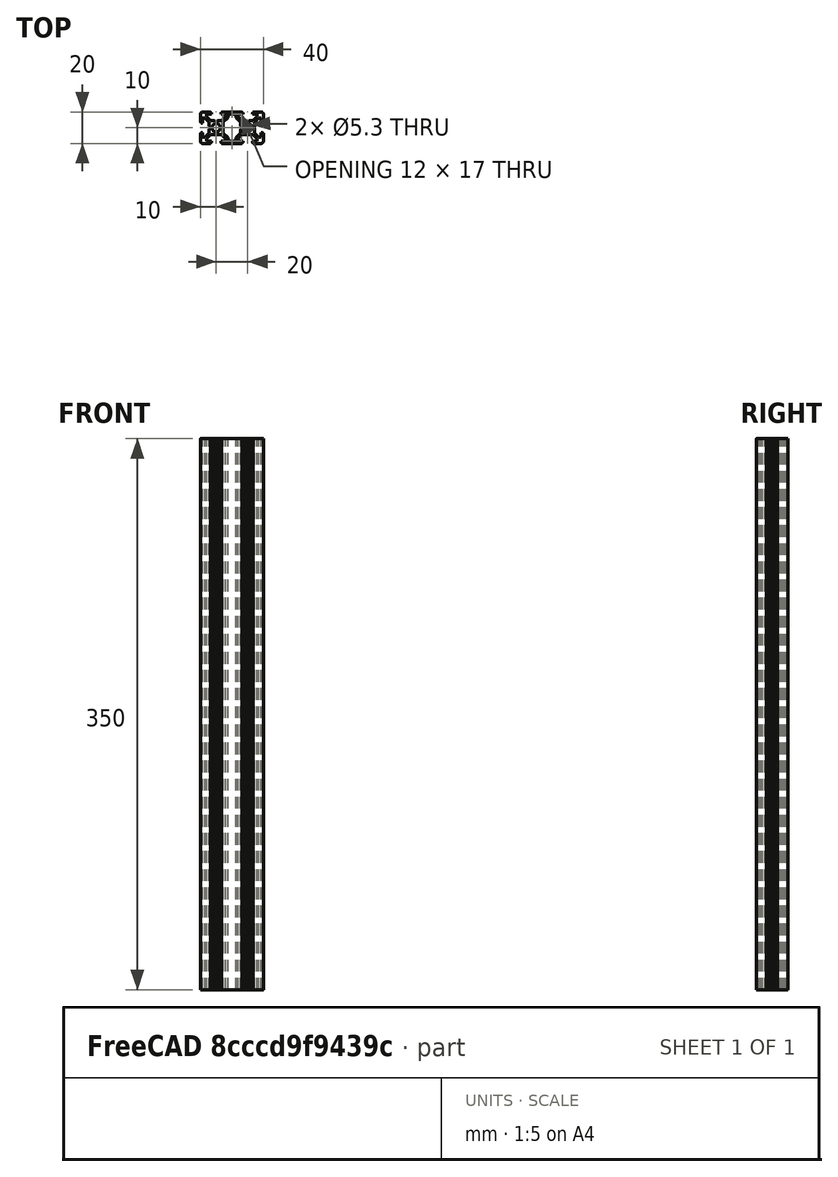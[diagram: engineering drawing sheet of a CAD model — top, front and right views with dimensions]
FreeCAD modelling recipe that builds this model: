
FCSTD DOCUMENT  (FreeCAD 0.17R13541 (Git))
Label: xx_458_aluminimum-extrusion
License: All rights reserved
LicenseURL: http://en.wikipedia.org/wiki/All_rights_reserved
objects: Sketcher::SketchObject×1, PartDesign::Pad×1, PartDesign::Body×1, Part::Feature×1
note: 5 computed .brp shape members not serialized (recipe doc carries the construction recipe); baked Part::Feature solids carry a one-line shape summary decoded from their .brp

FEATURE [Sketcher::SketchObject] Sketch516
  sketch-geometry (130):
    g0: LineSegment StartX=17.0607 StartY=-6 StartZ=0 EndX=14.5 EndY=-3.43934 EndZ=0
    g1: LineSegment StartX=16 StartY=-7.06066 StartZ=0 EndX=13.4393 EndY=-4.5 EndZ=0
    g2: LineSegment StartX=-4 StartY=-7.06066 StartZ=0 EndX=-6.56066 EndY=-4.5 EndZ=0
    g3: LineSegment StartX=6.56066 StartY=4.5 StartZ=0 EndX=4 EndY=7.06066 EndZ=0
    g4: LineSegment StartX=14.5 StartY=-0.866025 StartZ=0 EndX=14 EndY=0 EndZ=0
    g5: LineSegment StartX=-13.4393 StartY=4.5 StartZ=0 EndX=-16 EndY=7.06066 EndZ=0
    g6: LineSegment StartX=-18.5 StartY=-10 StartZ=0 EndX=-13.5 EndY=-10 EndZ=0
    g7: LineSegment StartX=13.5 StartY=-10 StartZ=0 EndX=18.5 EndY=-10 EndZ=0
    g8: LineSegment StartX=-6.5 StartY=-10 StartZ=0 EndX=6.5 EndY=-10 EndZ=0
    g9: LineSegment StartX=6 StartY=0 StartZ=0 EndX=5.5 EndY=0.866025 EndZ=0
    g10: LineSegment StartX=5.5 StartY=3.43934 StartZ=0 EndX=2.5 EndY=6.43934 EndZ=0
    g11: LineSegment StartX=-14 StartY=0 StartZ=0 EndX=-14.5 EndY=0.866025 EndZ=0
    g12: LineSegment StartX=10.866 StartY=-4.5 StartZ=0 EndX=10 EndY=-4 EndZ=0
    g13: LineSegment StartX=-9.13397 StartY=-4.5 StartZ=0 EndX=-10 EndY=-4 EndZ=0
    g14: LineSegment StartX=10 StartY=4 StartZ=0 EndX=9.13397 EndY=4.5 EndZ=0
    g15: LineSegment StartX=-10 StartY=4 StartZ=0 EndX=-10.866 EndY=4.5 EndZ=0
    g16: LineSegment StartX=-2.5 StartY=-6.43934 StartZ=0 EndX=-5.5 EndY=-3.43934 EndZ=0
    g17: LineSegment StartX=-14.5 StartY=3.43934 StartZ=0 EndX=-17.0607 EndY=6 EndZ=0
    g18: LineSegment StartX=-6.5 StartY=10 StartZ=0 EndX=6.5 EndY=10 EndZ=0
    g19: LineSegment StartX=-5.5 StartY=-0.866025 StartZ=0 EndX=-6 EndY=0 EndZ=0
    g20: LineSegment StartX=-7 StartY=-9.5 StartZ=0 EndX=-6.5 EndY=-9.5 EndZ=0
    g21: LineSegment StartX=-13.5 StartY=-9.5 StartZ=0 EndX=-13 EndY=-9.5 EndZ=0
    g22: LineSegment StartX=-16 StartY=-8.5 StartZ=0 EndX=-13 EndY=-8.5 EndZ=0
    g23: LineSegment StartX=-2.5 StartY=-8.5 StartZ=0 EndX=2.5 EndY=-8.5 EndZ=0
    g24: LineSegment StartX=13 StartY=-9.5 StartZ=0 EndX=13.5 EndY=-9.5 EndZ=0
    g25: LineSegment StartX=-18.5 StartY=-6 StartZ=0 EndX=-17.0607 EndY=-6 EndZ=0
    g26: LineSegment StartX=6.5 StartY=-9.5 StartZ=0 EndX=7 EndY=-9.5 EndZ=0
    g27: LineSegment StartX=-7 StartY=-8.5 StartZ=0 EndX=-4 EndY=-8.5 EndZ=0
    g28: LineSegment StartX=13 StartY=-8.5 StartZ=0 EndX=16 EndY=-8.5 EndZ=0
    g29: LineSegment StartX=4 StartY=-8.5 StartZ=0 EndX=7 EndY=-8.5 EndZ=0
    g30: LineSegment StartX=17.0607 StartY=-6 StartZ=0 EndX=18.5 EndY=-6 EndZ=0
    g31: LineSegment StartX=-13.4393 StartY=-4.5 StartZ=0 EndX=-10.866 EndY=-4.5 EndZ=0
    g32: LineSegment StartX=-9.13397 StartY=-4.5 StartZ=0 EndX=-6.56066 EndY=-4.5 EndZ=0
    g33: LineSegment StartX=6.56066 StartY=-4.5 StartZ=0 EndX=9.13397 EndY=-4.5 EndZ=0
    g34: LineSegment StartX=-20 StartY=-3.5 StartZ=0 EndX=-19.5 EndY=-3.5 EndZ=0
    g35: LineSegment StartX=10.866 StartY=-4.5 StartZ=0 EndX=13.4393 EndY=-4.5 EndZ=0
    g36: LineSegment StartX=19.5 StartY=-3.5 StartZ=0 EndX=20 EndY=-3.5 EndZ=0
    g37: LineSegment StartX=-19.5 StartY=-3 StartZ=0 EndX=-18.5 EndY=-3 EndZ=0
    g38: LineSegment StartX=18.5 StartY=-3 StartZ=0 EndX=19.5 EndY=-3 EndZ=0
    g39: LineSegment StartX=-19.5 StartY=3 StartZ=0 EndX=-18.5 EndY=3 EndZ=0
    g40: LineSegment StartX=18.5 StartY=3 StartZ=0 EndX=19.5 EndY=3 EndZ=0
    g41: LineSegment StartX=-20 StartY=3.5 StartZ=0 EndX=-19.5 EndY=3.5 EndZ=0
    g42: LineSegment StartX=19.5 StartY=3.5 StartZ=0 EndX=20 EndY=3.5 EndZ=0
    g43: LineSegment StartX=6.56066 StartY=4.5 StartZ=0 EndX=9.13397 EndY=4.5 EndZ=0
    g44: LineSegment StartX=-9.13397 StartY=4.5 StartZ=0 EndX=-6.56066 EndY=4.5 EndZ=0
    g45: LineSegment StartX=-13.4393 StartY=4.5 StartZ=0 EndX=-10.866 EndY=4.5 EndZ=0
    g46: LineSegment StartX=-18.5 StartY=6 StartZ=0 EndX=-17.0607 EndY=6 EndZ=0
    g47: LineSegment StartX=10.866 StartY=4.5 StartZ=0 EndX=13.4393 EndY=4.5 EndZ=0
    g48: LineSegment StartX=-16 StartY=8.5 StartZ=0 EndX=-13 EndY=8.5 EndZ=0
    g49: LineSegment StartX=17.0607 StartY=6 StartZ=0 EndX=18.5 EndY=6 EndZ=0
    g50: LineSegment StartX=4 StartY=8.5 StartZ=0 EndX=7 EndY=8.5 EndZ=0
    g51: LineSegment StartX=-7 StartY=8.5 StartZ=0 EndX=-4 EndY=8.5 EndZ=0
    g52: LineSegment StartX=-7 StartY=9.5 StartZ=0 EndX=-6.5 EndY=9.5 EndZ=0
    g53: LineSegment StartX=13 StartY=8.5 StartZ=0 EndX=16 EndY=8.5 EndZ=0
    g54: LineSegment StartX=-2.5 StartY=8.5 StartZ=0 EndX=2.5 EndY=8.5 EndZ=0
    g55: LineSegment StartX=6.5 StartY=9.5 StartZ=0 EndX=7 EndY=9.5 EndZ=0
    g56: LineSegment StartX=-13.5 StartY=9.5 StartZ=0 EndX=-13 EndY=9.5 EndZ=0
    g57: LineSegment StartX=13 StartY=9.5 StartZ=0 EndX=13.5 EndY=9.5 EndZ=0
    g58: LineSegment StartX=-18.5 StartY=10 StartZ=0 EndX=-13.5 EndY=10 EndZ=0
    g59: LineSegment StartX=13.5 StartY=10 StartZ=0 EndX=18.5 EndY=10 EndZ=0
    g60: LineSegment StartX=-10.866 StartY=-4.5 StartZ=0 EndX=-10 EndY=-4 EndZ=0
    g61: LineSegment StartX=9.13397 StartY=-4.5 StartZ=0 EndX=10 EndY=-4 EndZ=0
    g62: LineSegment StartX=10 StartY=4 StartZ=0 EndX=10.866 EndY=4.5 EndZ=0
    g63: LineSegment StartX=-10 StartY=4 StartZ=0 EndX=-9.13397 EndY=4.5 EndZ=0
    g64: LineSegment StartX=-16 StartY=-7.06066 StartZ=0 EndX=-13.4393 EndY=-4.5 EndZ=0
    g65: LineSegment StartX=-6.56066 StartY=4.5 StartZ=0 EndX=-4 EndY=7.06066 EndZ=0
    g66: LineSegment StartX=4 StartY=-7.06066 StartZ=0 EndX=6.56066 EndY=-4.5 EndZ=0
    g67: LineSegment StartX=2.5 StartY=-6.43934 StartZ=0 EndX=5.5 EndY=-3.43934 EndZ=0
    g68: LineSegment StartX=-5.5 StartY=3.43934 StartZ=0 EndX=-2.5 EndY=6.43934 EndZ=0
    g69: LineSegment StartX=14.5 StartY=3.43934 StartZ=0 EndX=17.0607 EndY=6 EndZ=0
    g70: LineSegment StartX=-17.0607 StartY=-6 StartZ=0 EndX=-14.5 EndY=-3.43934 EndZ=0
    g71: LineSegment StartX=13.4393 StartY=4.5 StartZ=0 EndX=16 EndY=7.06066 EndZ=0
    g72: LineSegment StartX=5.5 StartY=-0.866025 StartZ=0 EndX=6 EndY=0 EndZ=0
    g73: LineSegment StartX=-14.5 StartY=-0.866025 StartZ=0 EndX=-14 EndY=0 EndZ=0
    g74: LineSegment StartX=14 StartY=0 StartZ=0 EndX=14.5 EndY=0.866025 EndZ=0
    g75: LineSegment StartX=-6 StartY=0 StartZ=0 EndX=-5.5 EndY=0.866025 EndZ=0
    g76: LineSegment StartX=-20 StartY=3.5 StartZ=0 EndX=-20 EndY=8.5 EndZ=0
    g77: LineSegment StartX=-20 StartY=-8.5 StartZ=0 EndX=-20 EndY=-3.5 EndZ=0
    g78: LineSegment StartX=-19.5 StartY=-3.5 StartZ=0 EndX=-19.5 EndY=-3 EndZ=0
    g79: LineSegment StartX=-19.5 StartY=3 StartZ=0 EndX=-19.5 EndY=3.5 EndZ=0
    g80: LineSegment StartX=-16 StartY=7.06066 StartZ=0 EndX=-16 EndY=8.5 EndZ=0
    g81: LineSegment StartX=-18.5 StartY=3 StartZ=0 EndX=-18.5 EndY=6 EndZ=0
    g82: LineSegment StartX=-18.5 StartY=-6 StartZ=0 EndX=-18.5 EndY=-3 EndZ=0
    g83: LineSegment StartX=-13.5 StartY=-10 StartZ=0 EndX=-13.5 EndY=-9.5 EndZ=0
    g84: LineSegment StartX=-16 StartY=-8.5 StartZ=0 EndX=-16 EndY=-7.06066 EndZ=0
    g85: LineSegment StartX=-14.5 StartY=0.866025 StartZ=0 EndX=-14.5 EndY=3.43934 EndZ=0
    g86: LineSegment StartX=-13 StartY=8.5 StartZ=0 EndX=-13 EndY=9.5 EndZ=0
    g87: LineSegment StartX=-14.5 StartY=-3.43934 StartZ=0 EndX=-14.5 EndY=-0.866025 EndZ=0
    g88: LineSegment StartX=-13.5 StartY=9.5 StartZ=0 EndX=-13.5 EndY=10 EndZ=0
    g89: LineSegment StartX=-13 StartY=-9.5 StartZ=0 EndX=-13 EndY=-8.5 EndZ=0
    g90: LineSegment StartX=-7 StartY=8.5 StartZ=0 EndX=-7 EndY=9.5 EndZ=0
    g91: LineSegment StartX=-7 StartY=-9.5 StartZ=0 EndX=-7 EndY=-8.5 EndZ=0
    g92: LineSegment StartX=-6.5 StartY=-10 StartZ=0 EndX=-6.5 EndY=-9.5 EndZ=0
    g93: LineSegment StartX=-6.5 StartY=9.5 StartZ=0 EndX=-6.5 EndY=10 EndZ=0
    g94: LineSegment StartX=-2.5 StartY=6.43934 StartZ=0 EndX=-2.5 EndY=8.5 EndZ=0
    g95: LineSegment StartX=-5.5 StartY=-3.43934 StartZ=0 EndX=-5.5 EndY=-0.866025 EndZ=0
    g96: LineSegment StartX=-5.5 StartY=0.866025 StartZ=0 EndX=-5.5 EndY=3.43934 EndZ=0
    g97: LineSegment StartX=-4 StartY=-8.5 StartZ=0 EndX=-4 EndY=-7.06066 EndZ=0
    g98: LineSegment StartX=-4 StartY=7.06066 StartZ=0 EndX=-4 EndY=8.5 EndZ=0
    g99: LineSegment StartX=-2.5 StartY=-8.5 StartZ=0 EndX=-2.5 EndY=-6.43934 EndZ=0
    g100: LineSegment StartX=2.5 StartY=-8.5 StartZ=0 EndX=2.5 EndY=-6.43934 EndZ=0
    g101: LineSegment StartX=2.5 StartY=6.43934 StartZ=0 EndX=2.5 EndY=8.5 EndZ=0
    g102: LineSegment StartX=4 StartY=7.06066 StartZ=0 EndX=4 EndY=8.5 EndZ=0
    g103: LineSegment StartX=5.5 StartY=-3.43934 StartZ=0 EndX=5.5 EndY=-0.866025 EndZ=0
    g104: LineSegment StartX=5.5 StartY=0.866025 StartZ=0 EndX=5.5 EndY=3.43934 EndZ=0
    g105: LineSegment StartX=4 StartY=-8.5 StartZ=0 EndX=4 EndY=-7.06066 EndZ=0
    g106: LineSegment StartX=6.5 StartY=9.5 StartZ=0 EndX=6.5 EndY=10 EndZ=0
    g107: LineSegment StartX=7 StartY=8.5 StartZ=0 EndX=7 EndY=9.5 EndZ=0
    g108: LineSegment StartX=7 StartY=-9.5 StartZ=0 EndX=7 EndY=-8.5 EndZ=0
    g109: LineSegment StartX=6.5 StartY=-10 StartZ=0 EndX=6.5 EndY=-9.5 EndZ=0
    g110: LineSegment StartX=13 StartY=-9.5 StartZ=0 EndX=13 EndY=-8.5 EndZ=0
    g111: LineSegment StartX=13 StartY=8.5 StartZ=0 EndX=13 EndY=9.5 EndZ=0
    g112: LineSegment StartX=13.5 StartY=-10 StartZ=0 EndX=13.5 EndY=-9.5 EndZ=0
    g113: LineSegment StartX=14.5 StartY=0.866025 StartZ=0 EndX=14.5 EndY=3.43934 EndZ=0
    g114: LineSegment StartX=13.5 StartY=9.5 StartZ=0 EndX=13.5 EndY=10 EndZ=0
    g115: LineSegment StartX=14.5 StartY=-3.43934 StartZ=0 EndX=14.5 EndY=-0.866025 EndZ=0
    g116: LineSegment StartX=16 StartY=-8.5 StartZ=0 EndX=16 EndY=-7.06066 EndZ=0
    g117: LineSegment StartX=16 StartY=7.06066 StartZ=0 EndX=16 EndY=8.5 EndZ=0
    g118: LineSegment StartX=18.5 StartY=-6 StartZ=0 EndX=18.5 EndY=-3 EndZ=0
    g119: LineSegment StartX=19.5 StartY=-3.5 StartZ=0 EndX=19.5 EndY=-3 EndZ=0
    g120: LineSegment StartX=19.5 StartY=3 StartZ=0 EndX=19.5 EndY=3.5 EndZ=0
    g121: LineSegment StartX=18.5 StartY=3 StartZ=0 EndX=18.5 EndY=6 EndZ=0
    g122: LineSegment StartX=20 StartY=-8.5 StartZ=0 EndX=20 EndY=-3.5 EndZ=0
    g123: LineSegment StartX=20 StartY=3.5 StartZ=0 EndX=20 EndY=8.5 EndZ=0
    g124: ArcOfCircle CenterX=-18.5 CenterY=8.5 CenterZ=0 NormalX=0 NormalY=0 NormalZ=1 AngleXU=0 Radius=1.5 StartAngle=1.5708 EndAngle=3.14159
    g125: ArcOfCircle CenterX=18.5 CenterY=8.5 CenterZ=0 NormalX=0 NormalY=0 NormalZ=1 AngleXU=0 Radius=1.5 StartAngle=0 EndAngle=1.5708
    g126: ArcOfCircle CenterX=18.5 CenterY=-8.5 CenterZ=0 NormalX=0 NormalY=0 NormalZ=1 AngleXU=0 Radius=1.5 StartAngle=4.71239 EndAngle=6.28319
    g127: ArcOfCircle CenterX=-18.5 CenterY=-8.5 CenterZ=0 NormalX=0 NormalY=0 NormalZ=1 AngleXU=0 Radius=1.5 StartAngle=3.14159 EndAngle=4.71239
    g128: Circle CenterX=-10 CenterY=0 CenterZ=0 NormalX=0 NormalY=0 NormalZ=1 AngleXU=0 Radius=2.65
    g129: Circle CenterX=10 CenterY=0 CenterZ=0 NormalX=0 NormalY=0 NormalZ=1 AngleXU=0 Radius=2.65
  constraints (163):
    c: Vertical(g77)
    c: Vertical(g76)
    c: Vertical(g123)
    c: Vertical(g122)
    c: Horizontal(g58)
    c: Horizontal(g6)
    c: Horizontal(g8)
    c: Horizontal(g18)
    c: Horizontal(g59)
    c: Horizontal(g7)
    c: Coincident(g34,g77)
    c: Coincident(g41,g76)
    c: Coincident(g34,g78)
    c: Coincident(g37,g78)
    c: Coincident(g39,g79)
    c: Coincident(g41,g79)
    c: Coincident(g25,g82)
    c: Coincident(g37,g82)
    c: Coincident(g81,g39)
    c: Coincident(g46,g81)
    c: Coincident(g70,g25)
    c: Coincident(g46,g17)
    c: Coincident(g84,g22)
    c: Coincident(g84,g64)
    c: Coincident(g80,g5)
    c: Coincident(g80,g48)
    c: Coincident(g87,g70)
    c: Coincident(g87,g73)
    c: Coincident(g85,g11)
    c: Coincident(g17,g85)
    c: Coincident(g11,g73)
    c: Coincident(g83,g6)
    c: Coincident(g83,g21)
    c: Coincident(g88,g56)
    c: Coincident(g88,g58)
    c: Coincident(g31,g64)
    c: Coincident(g45,g5)
    c: Coincident(g21,g89)
    c: Coincident(g89,g22)
    c: Coincident(g86,g48)
    c: Coincident(g86,g56)
    c: Coincident(g31,g60)
    c: Coincident(g15,g45)
    c: Coincident(g60,g13)
    c: Coincident(g15,g63)
    c: Coincident(g13,g32)
    c: Coincident(g44,g63)
    c: Coincident(g20,g91)
    c: Coincident(g91,g27)
    c: Coincident(g90,g51)
    c: Coincident(g90,g52)
    c: Coincident(g32,g2)
    c: Coincident(g44,g65)
    c: Coincident(g92,g8)
    c: Coincident(g20,g92)
    c: Coincident(g52,g93)
    c: Coincident(g93,g18)
    c: Coincident(g19,g75)
    c: Coincident(g95,g16)
    c: Coincident(g19,g95)
    c: Coincident(g75,g96)
    c: Coincident(g96,g68)
    c: Coincident(g97,g27)
    c: Coincident(g2,g97)
    c: Coincident(g65,g98)
    c: Coincident(g51,g98)
    c: Coincident(g99,g23)
    c: Coincident(g16,g99)
    c: Coincident(g94,g68)
    c: Coincident(g54,g94)
    c: Coincident(g100,g23)
    c: Coincident(g100,g67)
    c: Coincident(g101,g10)
    c: Coincident(g54,g101)
    c: Coincident(g29,g105)
    c: Coincident(g105,g66)
    c: Coincident(g3,g102)
    c: Coincident(g50,g102)
    c: Coincident(g67,g103)
    c: Coincident(g103,g72)
    c: Coincident(g104,g9)
    c: Coincident(g10,g104)
    c: Coincident(g9,g72)
    c: Coincident(g8,g109)
    c: Coincident(g109,g26)
    c: Coincident(g106,g55)
    c: Coincident(g106,g18)
    c: Coincident(g33,g66)
    c: Coincident(g3,g43)
    c: Coincident(g108,g26)
    c: Coincident(g29,g108)
    c: Coincident(g50,g107)
    c: Coincident(g107,g55)
    c: Coincident(g61,g33)
    c: Coincident(g14,g43)
    c: Coincident(g61,g12)
    c: Coincident(g62,g14)
    c: Coincident(g35,g12)
    c: Coincident(g47,g62)
    c: Coincident(g24,g110)
    c: Coincident(g110,g28)
    c: Coincident(g111,g53)
    c: Coincident(g111,g57)
    c: Coincident(g35,g1)
    c: Coincident(g47,g71)
    c: Coincident(g7,g112)
    c: Coincident(g24,g112)
    c: Coincident(g57,g114)
    c: Coincident(g114,g59)
    c: Coincident(g74,g4)
    c: Coincident(g115,g0)
    c: Coincident(g4,g115)
    c: Coincident(g74,g113)
    c: Coincident(g69,g113)
    c: Coincident(g28,g116)
    c: Coincident(g116,g1)
    c: Coincident(g117,g71)
    c: Coincident(g53,g117)
    c: Coincident(g0,g30)
    c: Coincident(g49,g69)
    c: Coincident(g30,g118)
    c: Coincident(g38,g118)
    c: Coincident(g40,g121)
    c: Coincident(g121,g49)
    c: Coincident(g119,g36)
    c: Coincident(g119,g38)
    c: Coincident(g120,g40)
    c: Coincident(g120,g42)
    c: Coincident(g122,g36)
    c: Coincident(g42,g123)
    c: DistanceX(g58) = -13.5
    c: DistanceY(g58) = 10
    c: DistanceX(g41) = -20
    c: DistanceY(g41) = 3.5
    c: DistanceX(g34) = -20
    c: DistanceY(g34) = -3.5
    c: DistanceX(g6) = -13.5
    c: DistanceY(g6) = -10
    c: DistanceX(g7) = 13.5
    c: DistanceY(g7) = -10
    c: DistanceX(g36) = 20
    c: DistanceY(g36) = -3.5
    c: DistanceX(g42) = 20
    c: DistanceY(g42) = 3.5
    c: DistanceX(g59) = 13.5
    c: DistanceY(g59) = 10
    c: Tangent(g76,g124) = 1.5708
    c: Tangent(g124,g58) = 1.5708
    c: Tangent(g127,g77) = 1.5708
    c: Tangent(g127,g6) = -1.5708
    c: Tangent(g126,g7) = -1.5708
    c: Tangent(g126,g122) = -1.5708
    c: Tangent(g123,g125) = -1.5708
    c: Tangent(g125,g59) = 1.5708
    c: Equal(g125,g126)
    c: Equal(g126,g124)
    c: Equal(g124,g127)
    c: Radius(g124) = 1.5
    c: Symmetric(g129,g128,g-1)
    c: PointOnObject(g128,g-1)
    c: Distance(g128,g129) = 20
    c: Radius(g128) = 2.65
    c: Equal(g128,g129)
FEATURE [PartDesign::Pad] Pad
  Length = 350
  Length2 = 100
  Profile = -> Sketch516
  Type = 0
FEATURE [PartDesign::Body] Body
  Group = -> [Sketch516,Pad]
  Origin = -> Origin
  Tip = -> Pad
FEATURE [Part::Feature] Pad001
  shape: bbox 40 x 20 x 350 mm, 132 faces (baked)
